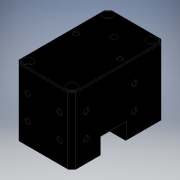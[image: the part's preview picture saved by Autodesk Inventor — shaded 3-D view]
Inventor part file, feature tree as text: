
AUTODESK INVENTOR PART (.ipt)
format: ipt  version: 2023 (Build 270158000, 158)  size: 558,080 bytes
history: native  units: mm
features: other x21, extrude x5, sketch x5
ambient origin geometry x8: Origin, YZ Plane, XZ Plane, XY Plane, X Axis, Y Axis, Z Axis, Center Point
bodies: Body1 (feature_tree)
feature tree (31):
  other  "ソリッド1"
  other  "作業平面1"
  extrude  "押し出し1"  Depth=0.5mm
  extrude  "押し出し2"  Depth=10.0mm TaperAngle=0.0deg
  extrude  "押し出し3"  Depth=15.0mm
  extrude  "押し出し4"  Depth=25.0mm
  extrude  "押し出し5"  Depth=20.0mm TaperAngle=0.0deg
  other  "ソリッド2"
  other  "ソリッド3"
  other  "ソリッド4"
  other  "ソリッド5"
  other  "ソリッド6"
  other  "ソリッド7"
  other  "ソリッド8"
  other  "ソリッド9"
  other  "ソリッド10"
  sketch  "スケッチ1"
  sketch  "スケッチ2"
  sketch  "スケッチ3"
  sketch  "スケッチ4"
  sketch  "スケッチ5"
  other  "X-430_IDLE_10:1"
  other  "X-430_SPACER_RING_11:1"
  other  "X-430_SPACER_RING_12:1"
  other  "X-430_SPACER_RING_13:1"
  other  "X-430_SPACER_RING_14:1"
  other  "X-430_SPACER_RING_15:1"
  other  "X-430_SPACER_RING_16:1"
  other  "X-430_SPACER_RING_17:1"
  other  "X-430_SPACER_RING_18:1"
  other  "X-430_CVR_CABLE_19:1"
